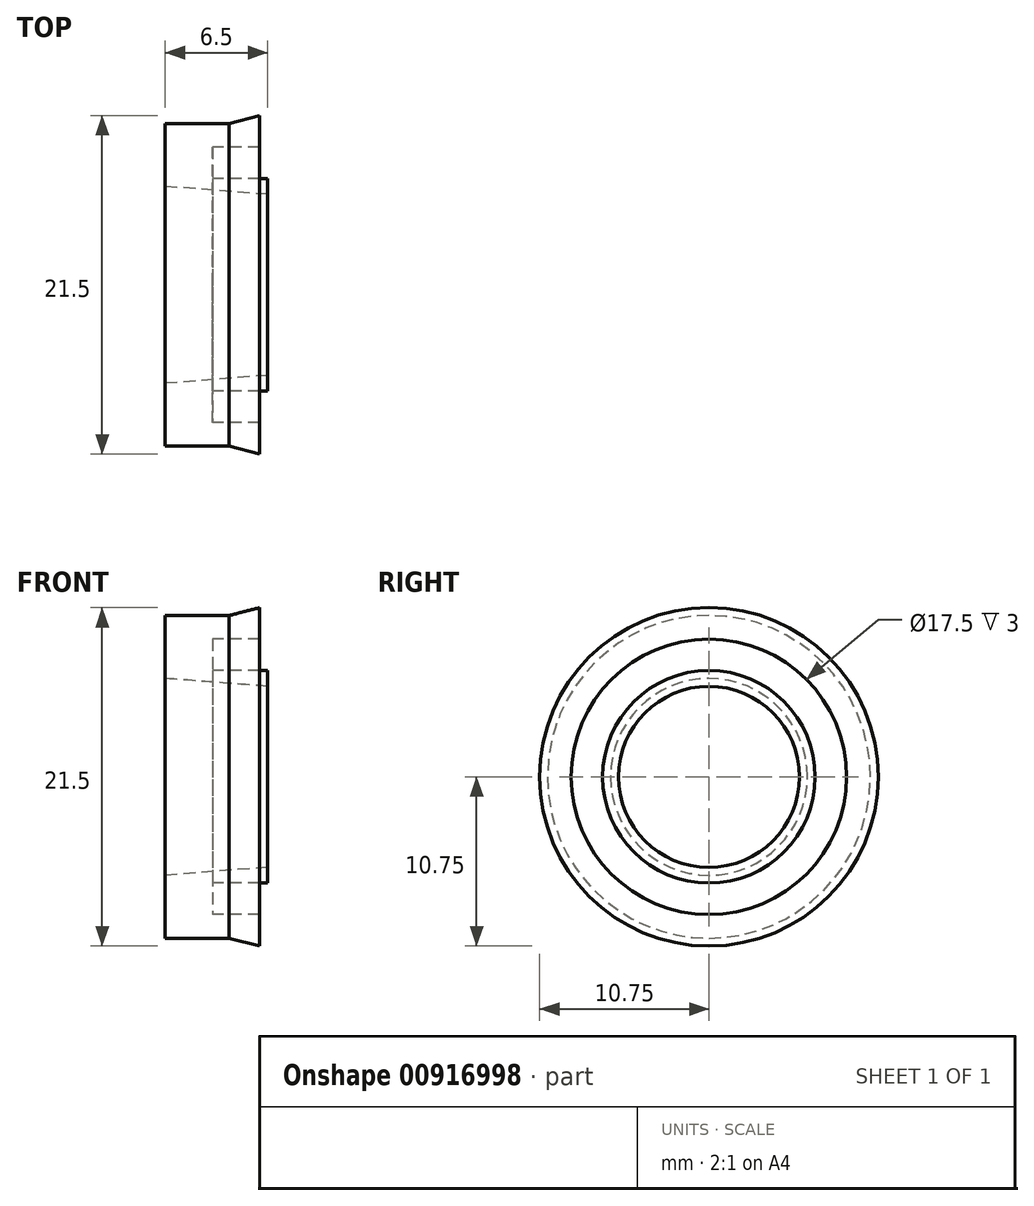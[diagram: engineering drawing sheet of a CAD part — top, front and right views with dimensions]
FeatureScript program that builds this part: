
annotation { "Feature Type Name" : "Feature", "Feature Type Description" : "" }
export const myFeature = defineFeature(function(context is Context, id is Id, definition is map)
    precondition{}
    {
        {
            var Q0;
            Q0=qCreatedBy(makeId("Front.planeOp"),FACE);
            var sketch = newSketch(context, id + "F0", { "sketchPlane" : qUnion([Q0])});
            skLineSegment(sketch, "E0", {"start": v(0, 0) * mm, "end": v(9.31, 0) * mm, "construction": true});
            skLineSegment(sketch, "E1", {"start": v(0, 0) * mm, "end": v(0, 10.75) * mm, "construction": true});
            skLineSegment(sketch, "E2", {"start": v(0, 10.75) * mm, "end": v(-1.94, 10.25) * mm});
            skLineSegment(sketch, "E3", {"start": v(-1.94, 10.25) * mm, "end": v(-6, 10.25) * mm});
            skLineSegment(sketch, "E4", {"start": v(-6, 10.25) * mm, "end": v(-6, 6.25) * mm});
            skLineSegment(sketch, "E5", {"start": v(-6, 6.25) * mm, "end": v(0.5, 5.75) * mm});
            skLineSegment(sketch, "E6", {"start": v(0.5, 5.75) * mm, "end": v(0.5, 6.75) * mm});
            skLineSegment(sketch, "E7", {"start": v(0.5, 6.75) * mm, "end": v(-3, 6.75) * mm});
            skLineSegment(sketch, "E8", {"start": v(-3, 6.75) * mm, "end": v(-3, 8.75) * mm});
            skLineSegment(sketch, "E9", {"start": v(-3, 8.75) * mm, "end": v(0, 8.75) * mm});
            skLineSegment(sketch, "E10", {"start": v(0, 8.75) * mm, "end": v(0, 10.75) * mm});
            skSolve(sketch);
        }
        {
            var Q0;
            Q0=makeQuery(id+"F0.imprint","IMPRINT",FACE,{"disambiguationData":[TD([[makeQuery(id+"F0.imprint","IMPRINT",EDGE,{"derivedFrom":sQuery(id+"F0.wireOp",EDGE,"E2")}),1.0]])]});
            var Q1;
            Q1=sQuery(id+"F0.wireOp",EDGE,"E0");
            revolve(context, id + "F1", {"surfaceOperationType" : NewSurfaceOperationType.NEW, "entities" : qUnion([Q0]), "axis" : qUnion([Q1]), "revolveType" : RevolveType.FULL});
        }
    });
